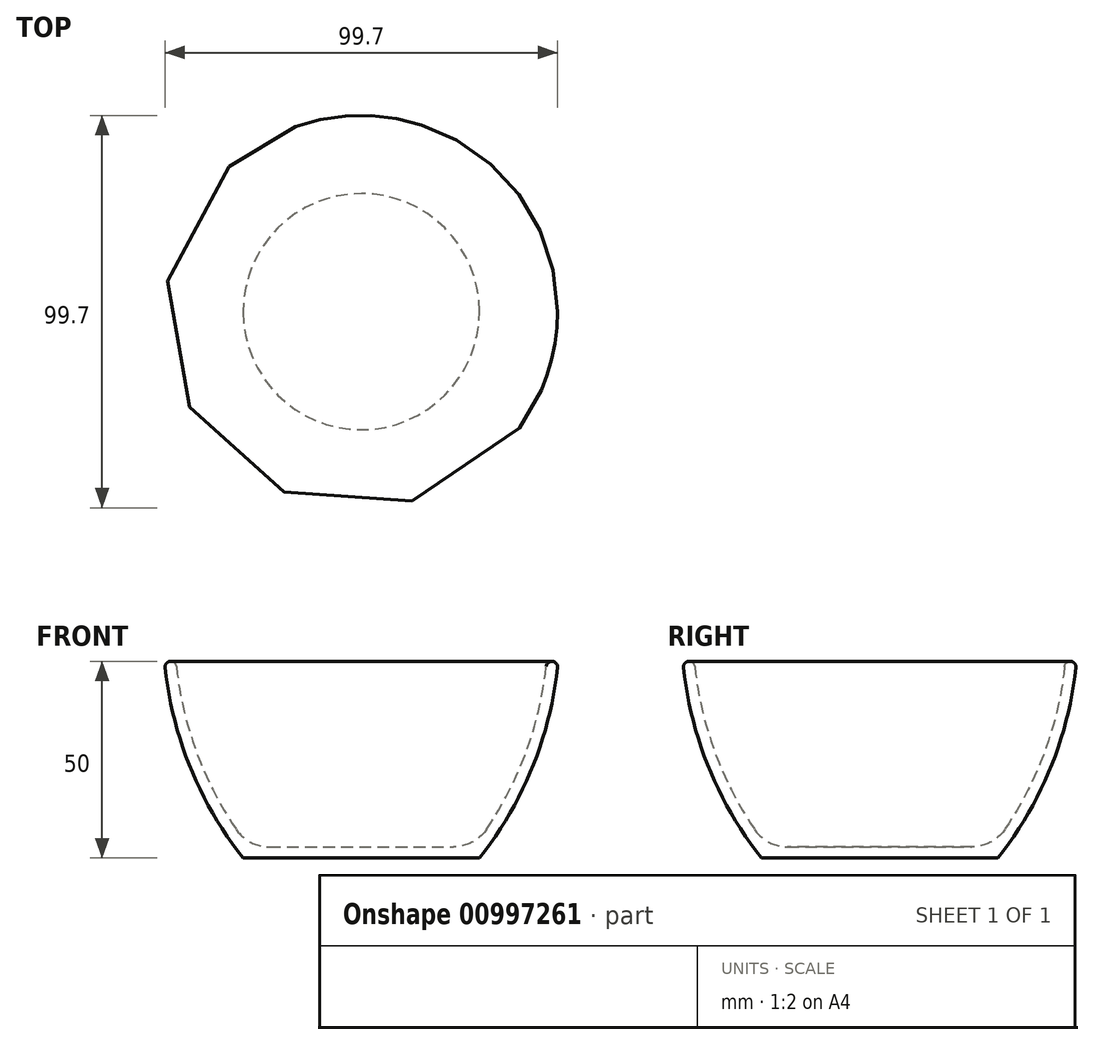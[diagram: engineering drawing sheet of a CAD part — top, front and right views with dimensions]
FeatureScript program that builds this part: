
annotation { "Feature Type Name" : "Feature", "Feature Type Description" : "" }
export const myFeature = defineFeature(function(context is Context, id is Id, definition is map)
    precondition{}
    {
        {
            assignVariable(context, id + "F0", {"name" : "wallthickness", "anyValue" : 0.72 * 4});
        }
        {
            var Q0;
            Q0=qCreatedBy(makeId("Front.planeOp"),FACE);
            var sketch = newSketch(context, id + "F1", { "sketchPlane" : qUnion([Q0])});
            skLineSegment(sketch, "E0", {"start": v(0, 0) * mm, "end": v(30, 0) * mm});
            skLineSegment(sketch, "E1", {"start": v(0, 0) * mm, "end": v(0, 50) * mm});
            skLineSegment(sketch, "E2", {"start": v(0, 50) * mm, "end": v(50, 50) * mm});
            skArc(sketch, "E3", {"start": v(30, 0) * mm, "mid": v(43.65, 23.54) * mm, "end": v(50, 50) * mm});
            skSolve(sketch);
        }
        {
            var Q0;
            Q0=makeQuery(id+"F1.imprint","IMPRINT",FACE,{"disambiguationData":[TD([[makeQuery(id+"F1.imprint","IMPRINT",EDGE,{"derivedFrom":sQuery(id+"F1.wireOp",EDGE,"E0")}),1.0]])]});
            var Q1;
            Q1=sQuery(id+"F1.wireOp",EDGE,"E1");
            revolve(context, id + "F2", {"surfaceOperationType" : NewSurfaceOperationType.NEW, "entities" : qUnion([Q0]), "axis" : qUnion([Q1]), "revolveType" : RevolveType.FULL});
        }
        {
            var Q0;
            Q0=makeQuery(id+"F2.opRevolve","SWEPT_FACE",FACE,{"disambiguationData":[OSD([sQuery(id+"F1.wireOp",EDGE,"E2")])]});
            shell(context, id + "F3", {"entities" : qUnion([Q0]), "thickness" : (getVariable(context, 'wallthickness')) * mm});
        }
        {
            var Q0;
            Q0=makeQuery(id+"F3.opShell","OFFSET_FACE",FACE,{"disambiguationData":[OSD([sQuery(id+"F1.wireOp",EDGE,"E0")])]});
            fillet(context, id + "F4", {"entities" : qUnion([Q0]), "radius" : 10 * mm, "tangentPropagation" : true, "allowEdgeOverflow" : false});
        }
        {
            var Q0;
            Q0=makeQuery(id+"F2.opRevolve","SWEPT_FACE",FACE,{"disambiguationData":[OSD([sQuery(id+"F1.wireOp",EDGE,"E2")])]});
            fillet(context, id + "F5", {"entities" : qUnion([Q0]), "radius" : (getVariable(context, 'wallthickness') / 2) * mm, "tangentPropagation" : true, "allowEdgeOverflow" : false});
        }
    });
